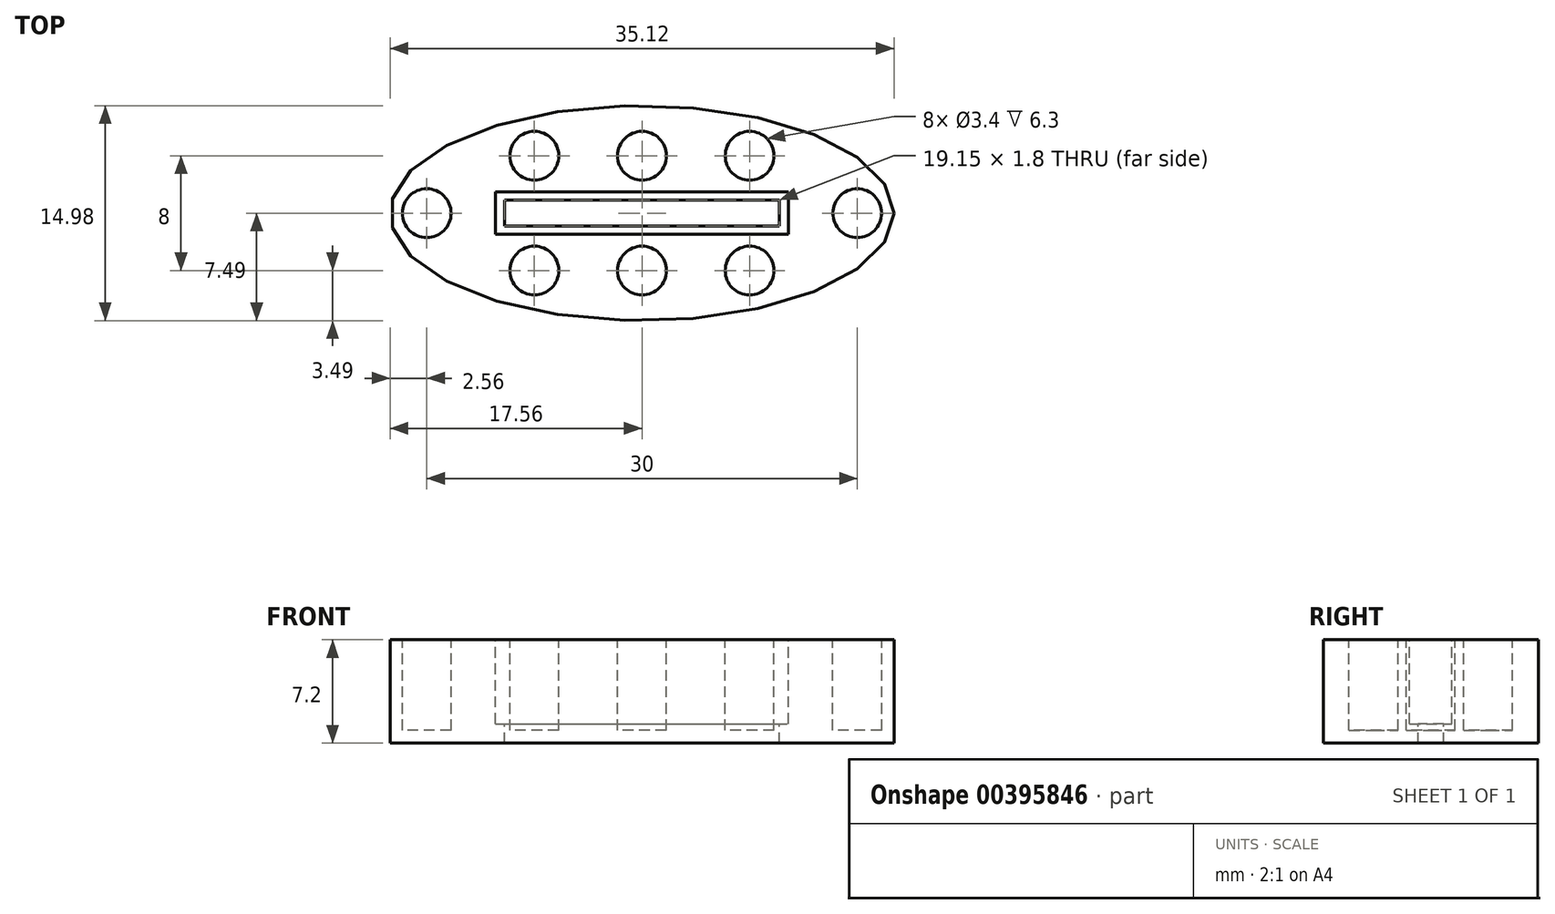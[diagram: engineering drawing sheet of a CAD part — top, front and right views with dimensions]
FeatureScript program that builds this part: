
annotation { "Feature Type Name" : "Feature", "Feature Type Description" : "" }
export const myFeature = defineFeature(function(context is Context, id is Id, definition is map)
    precondition{}
    {
        {
            var Q0;
            Q0=qCreatedBy(makeId("Top.planeOp"),FACE);
            var sketch = newSketch(context, id + "F0", { "sketchPlane" : qUnion([Q0])});
            skEllipse(sketch, "E0", {"center": v(0, 0) * mm, "majorRadius": 17.56 * mm, "minorRadius": 7.5 * mm, "majorAxis": v(1, 0)});
            skPoint(sketch, "E1", {"position": v(0, 7.5) * mm});
            skPoint(sketch, "E2", {"position": v(0, -7.5) * mm});
            skSolve(sketch);
        }
        {
            var Q0;
            Q0 = qSketchRegion(id + "F0", true);
            extrude(context, id + "F1", {"entities" : qUnion([Q0]), "depth" : 7.2 * mm});
        }
        {
            var Q0;
            Q0=makeQuery(id+"F1.opExtrude","CAP_FACE",FACE,{"disambiguationData":[OSD([sQuery(id+"F0.wireOp",EDGE,"E0")])],"isStart":false});
            var sketch = newSketch(context, id + "F2", { "sketchPlane" : qUnion([Q0])});
            skLineSegment(sketch, "E3.bottom", {"start": v(-10.2, -1.47) * mm, "end": v(10.2, -1.47) * mm});
            skLineSegment(sketch, "E3.top", {"start": v(-10.2, 1.47) * mm, "end": v(10.2, 1.47) * mm});
            skLineSegment(sketch, "E3.left", {"start": v(-10.2, -1.47) * mm, "end": v(-10.2, 1.47) * mm});
            skLineSegment(sketch, "E3.right", {"start": v(10.2, -1.47) * mm, "end": v(10.2, 1.47) * mm});
            skPoint(sketch, "E3.middle", {"position": v(0, 0) * mm});
            skSolve(sketch);
        }
        {
            var Q0;
            Q0 = qSketchRegion(id + "F2", true);
            var Q1;
            Q1 = qSketchRegion(id + "F4", true);
            extrude(context, id + "F3", {"entities" : qUnion([Q0, Q1]), "operationType" : NewBodyOperationType.REMOVE, "oppositeDirection" : true, "depth" : 5.85 * mm});
        }
        {
            var Q0;
            Q0=makeQuery(id+"F3.boolean.opBoolean","COPY",FACE,{"derivedFrom":makeQuery(id+"F3.opExtrude","CAP_FACE",FACE,{"disambiguationData":[OSD([sQuery(id+"F2.wireOp",EDGE,"E3.bottom"),sQuery(id+"F2.wireOp",EDGE,"E3.top"),sQuery(id+"F2.wireOp",EDGE,"E3.left"),sQuery(id+"F2.wireOp",EDGE,"E3.right")])],"isStart":false})});
            var sketch = newSketch(context, id + "F4", { "sketchPlane" : qUnion([Q0])});
            skLineSegment(sketch, "E4.bottom", {"start": v(-9.57, 0.9) * mm, "end": v(9.57, 0.9) * mm});
            skLineSegment(sketch, "E4.top", {"start": v(-9.57, -0.9) * mm, "end": v(9.57, -0.9) * mm});
            skLineSegment(sketch, "E4.left", {"start": v(-9.57, 0.9) * mm, "end": v(-9.57, -0.9) * mm});
            skLineSegment(sketch, "E4.right", {"start": v(9.57, 0.9) * mm, "end": v(9.57, -0.9) * mm});
            skPoint(sketch, "E4.middle", {"position": v(0, 0) * mm});
            skSolve(sketch);
        }
        {
            var Q0;
            Q0 = qSketchRegion(id + "F4", true);
            extrude(context, id + "F5", {"entities" : qUnion([Q0]), "operationType" : NewBodyOperationType.REMOVE, "endBound" : BoundingType.THROUGH_ALL, "oppositeDirection" : true, "depth" : 25 * mm});
        }
        {
            var Q0;
            Q0=makeQuery(id+"F1.opExtrude","CAP_FACE",FACE,{"disambiguationData":[OSD([sQuery(id+"F0.wireOp",EDGE,"E0")])],"isStart":false});
            var sketch = newSketch(context, id + "F6", { "sketchPlane" : qUnion([Q0])});
            skPoint(sketch, "E5", {"position": v(15, 0) * mm});
            skPoint(sketch, "E6", {"position": v(-15, 0) * mm});
            skPoint(sketch, "E7", {"position": v(0, 4) * mm});
            skPoint(sketch, "E8", {"position": v(0, -4) * mm});
            skCircle(sketch, "E9", {"center": v(-15, 0) * mm, "radius": 1.7 * mm});
            skCircle(sketch, "E10", {"center": v(0, -4) * mm, "radius": 1.7 * mm});
            skCircle(sketch, "E11", {"center": v(0, 4) * mm, "radius": 1.7 * mm});
            skCircle(sketch, "E12", {"center": v(15, 0) * mm, "radius": 1.7 * mm});
            skPoint(sketch, "E13", {"position": v(0, -0.95) * mm});
            skPoint(sketch, "E14", {"position": v(0, 1.47) * mm});
            skPoint(sketch, "E15", {"position": v(0, -1.47) * mm});
            skPoint(sketch, "E16", {"position": v(-10.2, 0) * mm});
            skPoint(sketch, "E17", {"position": v(10.2, 0) * mm});
            skPoint(sketch, "E18", {"position": v(-7.5, 4) * mm});
            skPoint(sketch, "E19", {"position": v(-7.5, -4) * mm});
            skPoint(sketch, "E20", {"position": v(7.5, 4) * mm});
            skPoint(sketch, "E21", {"position": v(7.5, -4) * mm});
            skCircle(sketch, "E22", {"center": v(-7.5, 4) * mm, "radius": 1.7 * mm});
            skCircle(sketch, "E23", {"center": v(-7.5, -4) * mm, "radius": 1.7 * mm});
            skCircle(sketch, "E24", {"center": v(7.5, -4) * mm, "radius": 1.7 * mm});
            skCircle(sketch, "E25", {"center": v(7.5, 4) * mm, "radius": 1.7 * mm});
            skPoint(sketch, "E26", {"position": v(-7.5, 0) * mm});
            skSolve(sketch);
        }
        {
            var Q0;
            Q0=makeQuery(id+"F6.imprint","IMPRINT",FACE,{"disambiguationData":[TD([[makeQuery(id+"F6.imprint","IMPRINT",EDGE,{"derivedFrom":sQuery(id+"F6.wireOp",EDGE,"E9")}),1.0]])]});
            var Q1;
            Q1=makeQuery(id+"F6.imprint","IMPRINT",FACE,{"disambiguationData":[TD([[makeQuery(id+"F6.imprint","IMPRINT",EDGE,{"derivedFrom":sQuery(id+"F6.wireOp",EDGE,"E11")}),1.0]])]});
            var Q2;
            Q2=makeQuery(id+"F6.imprint","IMPRINT",FACE,{"disambiguationData":[TD([[makeQuery(id+"F6.imprint","IMPRINT",EDGE,{"derivedFrom":sQuery(id+"F6.wireOp",EDGE,"E10")}),1.0]])]});
            var Q3;
            Q3=makeQuery(id+"F6.imprint","IMPRINT",FACE,{"disambiguationData":[TD([[makeQuery(id+"F6.imprint","IMPRINT",EDGE,{"derivedFrom":sQuery(id+"F6.wireOp",EDGE,"E12")}),1.0]])]});
            var Q4;
            Q4=makeQuery(id+"F6.imprint","IMPRINT",FACE,{"disambiguationData":[TD([[makeQuery(id+"F6.imprint","IMPRINT",EDGE,{"derivedFrom":sQuery(id+"F6.wireOp",EDGE,"E22")}),1.0]])]});
            var Q5;
            Q5=makeQuery(id+"F6.imprint","IMPRINT",FACE,{"disambiguationData":[TD([[makeQuery(id+"F6.imprint","IMPRINT",EDGE,{"derivedFrom":sQuery(id+"F6.wireOp",EDGE,"E25")}),1.0]])]});
            var Q6;
            Q6=makeQuery(id+"F6.imprint","IMPRINT",FACE,{"disambiguationData":[TD([[makeQuery(id+"F6.imprint","IMPRINT",EDGE,{"derivedFrom":sQuery(id+"F6.wireOp",EDGE,"E24")}),1.0]])]});
            var Q7;
            Q7=makeQuery(id+"F6.imprint","IMPRINT",FACE,{"disambiguationData":[TD([[makeQuery(id+"F6.imprint","IMPRINT",EDGE,{"derivedFrom":sQuery(id+"F6.wireOp",EDGE,"E23")}),1.0]])]});
            var Q8;
            Q8=sQuery(id+"F6.wireOp",EDGE,"E9");
            extrude(context, id + "F7", {"entities" : qUnion([Q0, Q1, Q2, Q3, Q4, Q5, Q6, Q7]), "operationType" : NewBodyOperationType.REMOVE, "surfaceEntities" : qUnion([Q8]), "oppositeDirection" : true, "depth" : 6.3 * mm});
        }
    });
